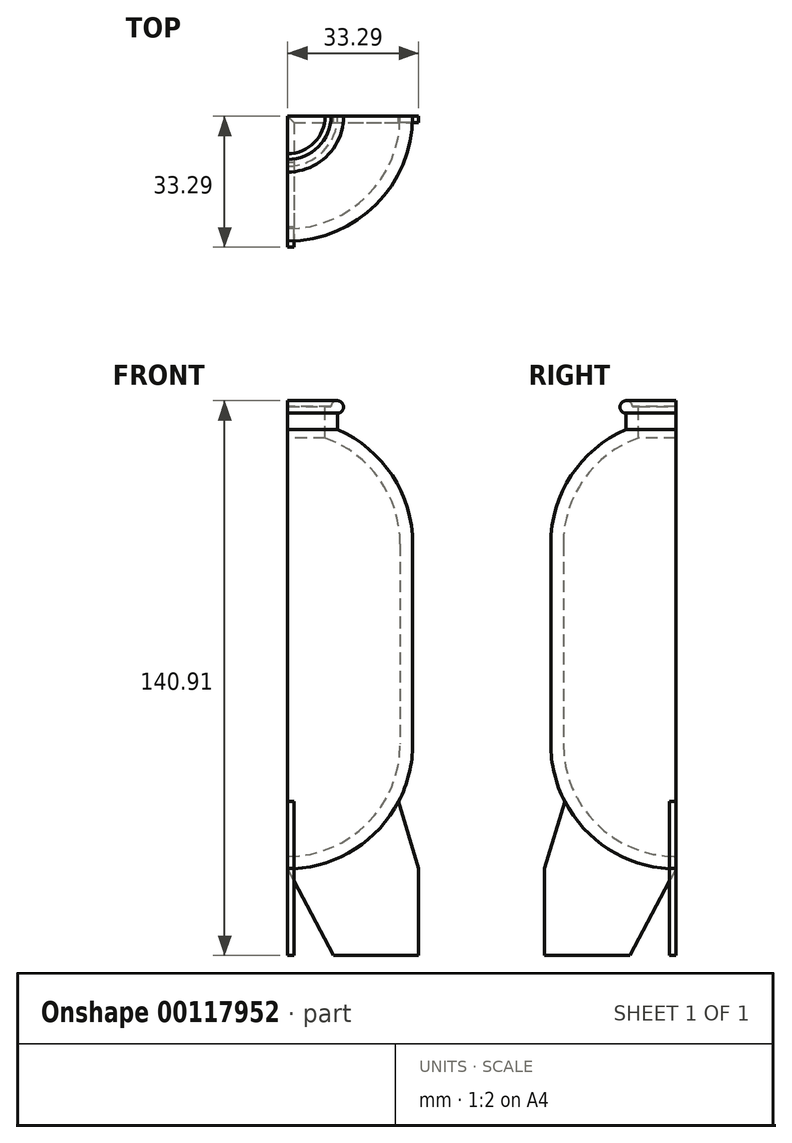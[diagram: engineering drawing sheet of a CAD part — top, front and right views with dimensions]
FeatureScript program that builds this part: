
annotation { "Feature Type Name" : "Feature", "Feature Type Description" : "" }
export const myFeature = defineFeature(function(context is Context, id is Id, definition is map)
    precondition{}
    {
        {
            var Q0;
            Q0=qCreatedBy(makeId("Top.planeOp"),FACE);
            var sketch = newSketch(context, id + "F0", { "sketchPlane" : qUnion([Q0])});
            skCircle(sketch, "E0", {"center": v(0, 0) * mm, "radius": 31.75 * mm});
            skCircle(sketch, "E1", {"center": v(0, 0) * mm, "radius": 28.58 * mm});
            skSolve(sketch);
        }
        {
            var Q0;
            Q0=qSketchRegion(id+"F0",true);
            extrude(context, id + "F1", {"entities" : qUnion([Q0]), "endBound" : BoundingType.SYMMETRIC, "depth" : 50.8 * mm});
        }
        {
            var Q0;
            Q0=makeQuery(id+"F1.opExtrude","CAP_FACE",FACE,{"disambiguationData":[OSD([sQuery(id+"F0.wireOp",EDGE,"E0"),sQuery(id+"F0.wireOp",EDGE,"E1")])],"isStart":false});
            var sketch = newSketch(context, id + "F2", { "sketchPlane" : qUnion([Q0])});
            skArc(sketch, "E2", {"start": v(0, -31.75) * mm, "mid": v(31.75, 0) * mm, "end": v(0, 31.75) * mm});
            skArc(sketch, "E3", {"start": v(0, -28.58) * mm, "mid": v(28.58, 0) * mm, "end": v(0, 28.58) * mm});
            skLineSegment(sketch, "E4", {"start": v(0, 31.75) * mm, "end": v(0, -31.75) * mm, "construction": true});
            skLineSegment(sketch, "E5", {"start": v(0, 31.75) * mm, "end": v(0, 28.58) * mm});
            skLineSegment(sketch, "E6", {"start": v(0, -31.75) * mm, "end": v(0, -28.58) * mm});
            skSolve(sketch);
        }
        {
            var Q0;
            Q0=qSketchRegion(id+"F2",true);
            var Q1;
            Q1=sQuery(id+"F2.wireOp",EDGE,"E4");
            revolve(context, id + "F3", {"operationType" : NewBodyOperationType.ADD, "entities" : qUnion([Q0]), "axis" : qUnion([Q1]), "revolveType" : RevolveType.ONE_DIRECTION, "angle" : 180 * degree});
        }
        {
            var Q0;
            Q0=makeQuery(id+"F1.opExtrude","SWEPT_BODY",BODY,{"disambiguationData":[OSD([sQuery(id+"F0.wireOp",EDGE,"E0"),sQuery(id+"F0.wireOp",EDGE,"E1")])]});
            var Q1;
            Q1=qCreatedBy(makeId("Top.planeOp"),FACE);
            mirror(context, id + "F4", {"operationType" : NewBodyOperationType.ADD, "entities" : qUnion([Q0]), "mirrorPlane" : qUnion([Q1])});
        }
        {
            var Q0;
            Q0=qCreatedBy(makeId("Top.planeOp"),FACE);
            cPlane(context, id + "F5", {"entities" : qUnion([Q0]), "cplaneType" : CPlaneType.OFFSET, "offset" : 57.15 * mm, "width" : 152.4 * mm, "height" : 152.4 * mm});
        }
        {
            var Q0;
            Q0=qCreatedBy(id+"F5.planeOp",FACE);
            var sketch = newSketch(context, id + "F6", { "sketchPlane" : qUnion([Q0])});
            skCircle(sketch, "E7", {"center": v(0, 0) * mm, "radius": 12.7 * mm});
            skSolve(sketch);
        }
        {
            var Q0;
            Q0=qSketchRegion(id+"F6",true);
            extrude(context, id + "F7", {"entities" : qUnion([Q0]), "operationType" : NewBodyOperationType.ADD, "endBound" : BoundingType.SYMMETRIC, "depth" : 6.35 * mm});
        }
        {
            var Q0;
            Q0=qCreatedBy(makeId("Top.planeOp"),FACE);
            cPlane(context, id + "F8", {"entities" : qUnion([Q0]), "cplaneType" : CPlaneType.OFFSET, "offset" : 57.15 * mm, "oppositeDirection" : true, "width" : 152.4 * mm, "height" : 152.4 * mm});
        }
        {
            var Q0;
            Q0=makeQuery(id+"F7.opExtrude","CAP_FACE",FACE,{"disambiguationData":[OSD([sQuery(id+"F6.wireOp",EDGE,"E7")])],"isStart":false});
            var sketch = newSketch(context, id + "F9", { "sketchPlane" : qUnion([Q0])});
            skCircle(sketch, "E8", {"center": v(0, 0) * mm, "radius": 9.53 * mm});
            skSolve(sketch);
        }
        {
            var Q0;
            Q0=qSketchRegion(id+"F9",true);
            extrude(context, id + "F10", {"entities" : qUnion([Q0]), "operationType" : NewBodyOperationType.REMOVE, "oppositeDirection" : true, "depth" : 25.4 * mm});
        }
        {
            var Q0;
            Q0=qCreatedBy(makeId("Front.planeOp"),FACE);
            var sketch = newSketch(context, id + "F11", { "sketchPlane" : qUnion([Q0])});
            skLineSegment(sketch, "E9", {"start": v(0, -57.15) * mm, "end": v(11.6, -79.09) * mm});
            skLineSegment(sketch, "E10", {"start": v(11.6, -79.09) * mm, "end": v(33.29, -79.09) * mm});
            skLineSegment(sketch, "E11", {"start": v(33.29, -79.09) * mm, "end": v(33.29, -57.05) * mm});
            skLineSegment(sketch, "E12", {"start": v(33.29, -57.05) * mm, "end": v(28.2, -40) * mm});
            skPoint(sketch, "E13.orphan", {"position": v(31.75, -25.4) * mm});
            skPoint(sketch, "E14.orphan", {"position": v(-31.75, -25.4) * mm});
            skLineSegment(sketch, "E15", {"start": v(28.2, -40) * mm, "end": v(27.19, -39.19) * mm});
            skArc(sketch, "E16.0", {"start": v(0, -56.61) * mm, "mid": v(14.18, -53.2) * mm, "end": v(25.27, -43.72) * mm});
            skLineSegment(sketch, "E17", {"start": v(27.19, -39.19) * mm, "end": v(25.27, -43.72) * mm});
            skLineSegment(sketch, "E18", {"start": v(0, -56.61) * mm, "end": v(0, -57.15) * mm});
            skSolve(sketch);
        }
        {
            var Q0;
            Q0=qSketchRegion(id+"F11",true);
            extrude(context, id + "F12", {"entities" : qUnion([Q0]), "operationType" : NewBodyOperationType.ADD, "endBound" : BoundingType.SYMMETRIC, "depth" : 3.17 * mm});
        }
        {
            var Q0;
            Q0=qCreatedBy(makeId("Front.planeOp"),FACE);
            var sketch = newSketch(context, id + "F13", { "sketchPlane" : qUnion([Q0])});
            skLineSegment(sketch, "E19", {"start": v(0, 72.95) * mm, "end": v(0, -20.55) * mm, "construction": true});
            skSolve(sketch);
        }
        {
            var Q0;
            Q0=makeQuery(id+"F1.opExtrude","SWEPT_BODY",BODY,{"disambiguationData":[OSD([sQuery(id+"F0.wireOp",EDGE,"E0"),sQuery(id+"F0.wireOp",EDGE,"E1")])]});
            var Q1;
            Q1=sQuery(id+"F13.wireOp",EDGE,"E19");
            circularPattern(context, id + "F14", {"entities" : qUnion([Q0]), "axis" : qUnion([Q1]), "angle" : 90 * degree, "instanceCount" : 4});
        }
        {
            var Q0;
            Q0=qCreatedBy(makeId("Front.planeOp"),FACE);
            var sketch = newSketch(context, id + "F15", { "sketchPlane" : qUnion([Q0])});
            skLineSegment(sketch, "E20", {"start": v(0, 46.85) * mm, "end": v(0, 31.4) * mm, "construction": true});
            skCircle(sketch, "E21", {"center": v(12.6, 60.23) * mm, "radius": 1.59 * mm});
            skSolve(sketch);
        }
        {
            var Q0;
            Q0=qSketchRegion(id+"F15",true);
            var Q1;
            Q1=sQuery(id+"F15.wireOp",EDGE,"E20");
            revolve(context, id + "F16", {"operationType" : NewBodyOperationType.ADD, "entities" : qUnion([Q0]), "axis" : qUnion([Q1]), "revolveType" : RevolveType.FULL});
        }
        {
            var Q0;
            Q0=qCreatedBy(id+"F5.planeOp",FACE);
            var sketch = newSketch(context, id + "F17", { "sketchPlane" : qUnion([Q0])});
            skLineSegment(sketch, "E22", {"start": v(0, -45.12) * mm, "end": v(0, 0) * mm});
            skLineSegment(sketch, "E23", {"start": v(0, 0) * mm, "end": v(39.38, 0) * mm});
            skLineSegment(sketch, "E24", {"start": v(39.38, 0) * mm, "end": v(39.38, 53.9) * mm});
            skLineSegment(sketch, "E25", {"start": v(39.38, 53.9) * mm, "end": v(-55.46, 53.9) * mm});
            skLineSegment(sketch, "E26", {"start": v(-55.46, 53.9) * mm, "end": v(-55.46, -47.21) * mm});
            skLineSegment(sketch, "E27", {"start": v(-55.46, -47.21) * mm, "end": v(0, -45.12) * mm});
            skSolve(sketch);
        }
        {
            var Q0;
            Q0 = qSketchRegion(id + "F17", true);
            extrude(context, id + "F18", {"entities" : qUnion([Q0]), "operationType" : NewBodyOperationType.REMOVE, "endBound" : BoundingType.THROUGH_ALL, "oppositeDirection" : true, "depth" : 25.4 * mm, "hasSecondDirection" : true, "secondDirectionOppositeDirection" : false, "secondDirectionDepth" : 25.4 * mm});
        }
    });
